# Revit family: E 1200 LUM
name_source: partatom
category: Lighting Fixtures
revit_build: Autodesk Revit 2017 (Build: 20160225_1515(x64)
units: mm (PartAtom-declared; Revit-internal decimal feet)

## family parameters
Cut with Voids When Loaded = No
Host = Face
Light Source = Yes
Part Type = Normal
Room Calculation Point = No
Round Connector Dimension = Use Diameter
Shared = No

## types (2) — shared parameters
Color Filter = 16777215
Default Elevation = 1219 mm
Dimming Lamp Color Temperature Shift = <None>
Emit Shape Visible in Rendering = Yes
Emit from Rectangle Length = 1126 mm  [stored 3.69423 ft]
Emit from Rectangle Width = 54 mm  [stored 0.177165 ft]
Lamp = LED
Manufacturer = ARLIGHT AYDINLATMA A.Ş.
Model = E1200LUM
Tilt Angle = 90.00°
Type Comments = Industrial Lighting
URL = arlight.net/en/products/indoor/industrial-lighting-fixtures/lumo

## per-type parameters (varying)
| type | Apparent Load | Photometric Web File | Wattage Comments |
| ELUM.1200.34.40 | 34 VA | e-1200-lum-34w-4k-80ra-rg-035.ies | 34W |
| ELUM.1200.24.40 | 24 VA | e-1200-lum-24w-4k-80ra-rg-025.ies | 24W |

note: [stored X ft] marks values corroborated as IEEE doubles in the binary element streams (Revit-internal decimal feet)

## geometry (parser evidence)
native form markers: Blend x4, Sweep x2
no freeform markers — native parametric forms only
